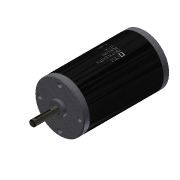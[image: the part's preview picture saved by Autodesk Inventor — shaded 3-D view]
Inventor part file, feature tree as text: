
AUTODESK INVENTOR PART (.ipt)
format: ipt  version: 2011 (Build 150239000, 239)  size: 470,016 bytes
history: native  units: in
note: dims shown in document units (in); Inventor stores cm internally (conversion verified against a paired STEP export)
features: sketch x20, extrude x15, projected_geometry x8, other x5, chamfer x4, plane x4, fillet x2, mirror x1, hole x1, revolve x1, pattern_circular x1
ambient origin geometry x8: Origin, YZ Plane, XZ Plane, XY Plane, X Axis, Y Axis, Z Axis, Center Point
bodies: Solid1 (feature_tree)
feature tree (62):
  extrude  "Extrusion1"  Depth=3.75in TaperAngle=0.0deg
  fillet  "Fillet1"  Radius=0.025in
  extrude  "Extrusion3"  Depth=0.035in TaperAngle=45.0deg
  mirror  "Mirror1"
  chamfer  "Chamfer1"  Distance=0.16in
  other  "Decal1"
  extrude  "Extrusion4"  Depth=4.0in TaperAngle=0.0deg
  extrude  "Extrusion5"  Depth=5.245in TaperAngle=0.0deg
  extrude  "Extrusion6"  TaperAngle=180.0deg  [1 undecoded]
  chamfer  "Chamfer2"  Distance=0.05in
  plane  "Work Plane1"
  extrude  "Extrusion7"  Depth=0.1815in TaperAngle=0.0deg
  extrude  "Extrusion8"  Depth=0.075in TaperAngle=45.0deg
  fillet  "Fillet2"  Radius=1.0in
  chamfer  "Chamfer3"  Distance=1.5748in Angle=360.0deg
  hole  "Hole1"  [1 undecoded]
  extrude  "Extrusion9"  Depth=0.404in
  plane  "Work Plane3"
  sketch  "Sketch11"  dims[d44=180.0deg]
  extrude  "Extrusion10"  TaperAngle=0.0deg  [1 undecoded]
  extrude  "Extrusion11"  Depth=1.987in
  extrude  "Extrusion12"  Depth=4.125in TaperAngle=0.0deg
  extrude  "Extrusion13"  Depth=0.375in TaperAngle=0.0deg
  extrude  "Extrusion14"  Depth=0.404in
  extrude  "Extrusion15"  TaperAngle=0.0deg  [1 undecoded]
  chamfer  "Chamfer4"  Distance=0.9935in
  plane  "Work Plane4"
  revolve  "Revolution1"  Angle=360.0deg
  extrude  "Extrusion16"  Depth=0.25in TaperAngle=0.0deg
  pattern_circular  "Circular Pattern1"  [2 undecoded]
  sketch  "Sketch20"  dims[d87=0.9935in d88=4.125in d89=0.0in d90=0.375in d91=0.0in d92=0.404in d93=0.0in d94=0.9935in d95=0.7874in d97=360.0deg d99=0.25in d100=0.0in d101=1.987in d102=0.125in d103=0.125in d104=3.875in d105=0.0in d106=0.409in d107=0.25in d108=0.22in d109=0.252in d110=0.314in d111=0.314in d112=0.096in d113=0.0in d114=0.144in d115=0.125in d116=0.0in d117=0.085in d118=0.125in d119=45.0deg d120=0.136in d121=0.136in d122=0.134in d123=90.0deg d124=0.075in d125=0.075in d126=0.0375in d127=0.0375in d128=0.125in d129=0.125in d130=0.125in d131=0.125in d132=0.1in d133=-0.2199in d134=0.7874in d135=360.0deg]
  sketch  "Sketch1"  dims[d0=2.5in d1=3.75in d2=0.0in d3=0.025in]
  sketch  "Sketch2"  dims[d7=0.287in d8=0.0in d9=0.035in d10=0.125in d11=45.0deg]
  projected_geometry  "Projected Loop1"
  sketch  "Sketch3"  dims[d21=1.3in]
  other  "Image1"
  projected_geometry  "Projected Loop2"
  sketch  "Sketch4"  dims[d22=1.1in]
  sketch  "Sketch5"  dims[d27=0.6in]
  sketch  "Sketch6"  dims[d28=0.75in d29=0.16in d30=0.0in]
  sketch  "Sketch7"  dims[d31=0.375in d32=4.0in d33=0.0in]
  sketch  "Sketch8"  dims[d35=0.3125in d36=5.245in d37=0.0in]
  sketch  "Sketch9"  dims[d39=0.04in d40=0.125in d41=45.0deg d42=180.0deg]
  projected_geometry  "Projected Loop3"
  sketch  "Sketch10"  dims[d43=0.075in]
  projected_geometry  "Projected Loop4"
  projected_geometry  "Projected Loop5"
  projected_geometry  "Projected Loop6"
  other  "Work Axis1"
  plane  "Work Plane2"
  sketch  "Sketch12"  dims[d45=0.7925in]
  sketch  "Sketch13"  dims[d46=0.185in d47=0.05in d48=0.0in]
  sketch  "Sketch14"  dims[d49=1.176in d50=0.1815in d51=0.0in]
  sketch  "Sketch15"  dims[d52=0.0125in d53=0.075in d54=0.125in d55=45.0deg d56=1.0in d57=1.5748in d59=360.0deg]
  sketch  "Sketch16"  dims[d61=0.13in d62=0.5in d63=0.25in d64=0.25in d65=0.5635in d66=0.5in d67=0.0in d68=0.425in d69=0.0in]
  sketch  "Sketch17"  dims[d71=90.0deg d82=0.404in]
  projected_geometry  "Projected Loop7"
  projected_geometry  "Projected Loop8"
  other  "Work Axis2"
  other  "Work Axis3"
  sketch  "Sketch18"  dims[d83=0.404in d84=0.0in]
  sketch  "Sketch19"  dims[d85=0.0in d86=1.987in]
note: 6 required parameter values undecoded (feature->parameter linkage not recoverable at this tier; creation-order binding heuristic only, values carry confidence <= 0.55)
